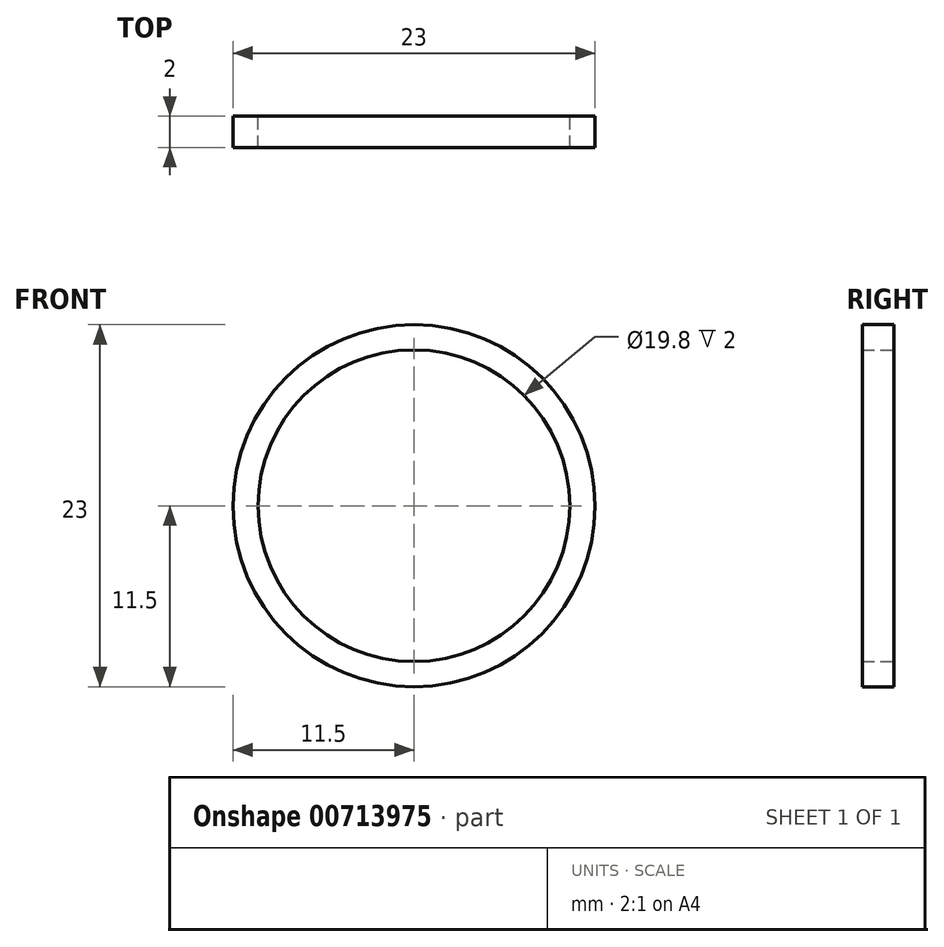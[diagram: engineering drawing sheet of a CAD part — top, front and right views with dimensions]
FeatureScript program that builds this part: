
annotation { "Feature Type Name" : "Feature", "Feature Type Description" : "" }
export const myFeature = defineFeature(function(context is Context, id is Id, definition is map)
    precondition{}
    {
        {
            var Q0;
            Q0=qCreatedBy(makeId("Front.planeOp"),FACE);
            var sketch = newSketch(context, id + "F0", { "sketchPlane" : qUnion([Q0])});
            skCircle(sketch, "E0", {"center": v(0, 0) * mm, "radius": 9.9 * mm});
            skCircle(sketch, "E1.0", {"center": v(0, 0) * mm, "radius": 11.5 * mm});
            skSolve(sketch);
        }
        {
            var Q0;
            Q0=makeQuery(id+"F0.imprint","IMPRINT",FACE,{"disambiguationData":[TD([[makeQuery(id+"F0.imprint","IMPRINT",EDGE,{"derivedFrom":sQuery(id+"F0.wireOp",EDGE,"E0")}),-1.0]])]});
            extrude(context, id + "F1", {"entities" : qUnion([Q0]), "depth" : 2 * mm, "offsetDistance" : 25 * mm});
        }
    });
